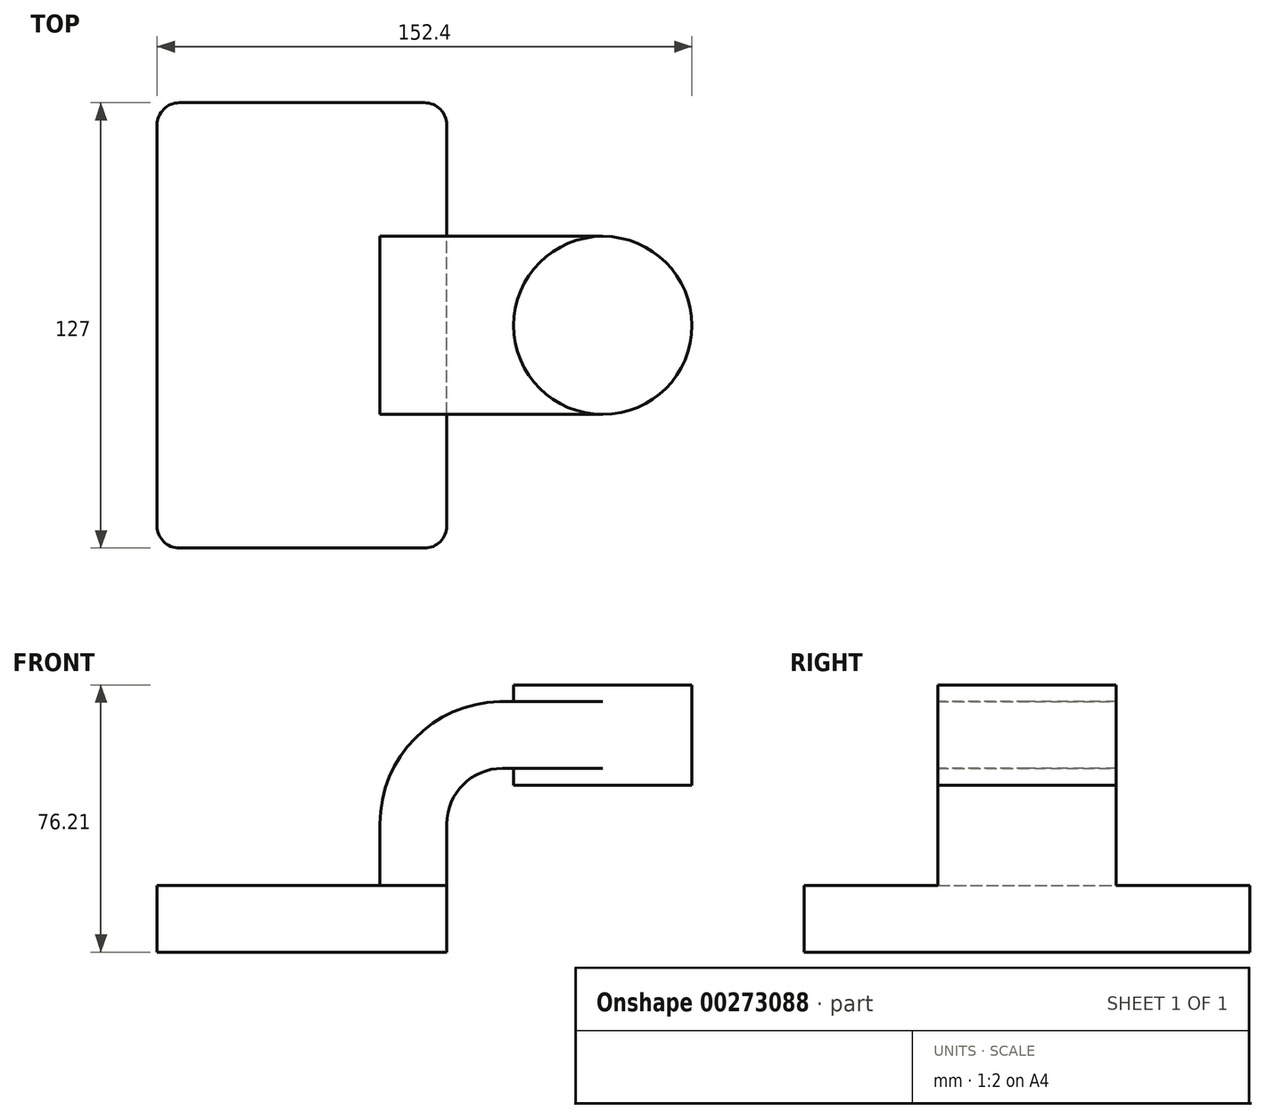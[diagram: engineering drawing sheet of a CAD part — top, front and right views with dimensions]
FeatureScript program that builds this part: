
annotation { "Feature Type Name" : "Feature", "Feature Type Description" : "" }
export const myFeature = defineFeature(function(context is Context, id is Id, definition is map)
    precondition{}
    {
        {
            var Q0;
            Q0=qCreatedBy(makeId("Front.planeOp"),FACE);
            var sketch = newSketch(context, id + "F0", { "sketchPlane" : qUnion([Q0])});
            skLineSegment(sketch, "E0.bottom", {"start": v(41.28, -9.52) * mm, "end": v(-41.28, -9.53) * mm});
            skLineSegment(sketch, "E0.top", {"start": v(41.28, 9.53) * mm, "end": v(-41.28, 9.52) * mm});
            skLineSegment(sketch, "E0.left", {"start": v(41.28, -9.52) * mm, "end": v(41.28, 9.53) * mm});
            skLineSegment(sketch, "E0.right", {"start": v(-41.28, -9.53) * mm, "end": v(-41.28, 9.52) * mm});
            skPoint(sketch, "E0.middle", {"position": v(0, 0) * mm});
            skLineSegment(sketch, "E1.bottom", {"start": v(111.12, 38.1) * mm, "end": v(60.32, 38.1) * mm});
            skLineSegment(sketch, "E1.top", {"start": v(111.12, 66.68) * mm, "end": v(60.32, 66.68) * mm});
            skLineSegment(sketch, "E1.left", {"start": v(111.12, 38.1) * mm, "end": v(111.12, 66.68) * mm});
            skLineSegment(sketch, "E1.right", {"start": v(60.32, 38.1) * mm, "end": v(60.32, 66.68) * mm});
            skPoint(sketch, "E1.middle", {"position": v(85.72, 52.39) * mm});
            skLineSegment(sketch, "E2", {"start": v(41.28, 9.53) * mm, "end": v(41.28, 27) * mm});
            skArc(sketch, "E3", {"start": v(57.15, 42.88) * mm, "mid": v(45.92, 38.23) * mm, "end": v(41.28, 27) * mm});
            skLineSegment(sketch, "E4", {"start": v(57.15, 42.88) * mm, "end": v(85.72, 42.88) * mm});
            skLineSegment(sketch, "E5.0", {"start": v(57.15, 61.93) * mm, "end": v(85.72, 61.93) * mm});
            skArc(sketch, "E5.1", {"start": v(57.15, 61.93) * mm, "mid": v(32.45, 51.7) * mm, "end": v(22.23, 27) * mm});
            skLineSegment(sketch, "E5.2", {"start": v(22.23, 9.53) * mm, "end": v(22.23, 27) * mm});
            skLineSegment(sketch, "E6", {"start": v(85.72, 38.1) * mm, "end": v(85.72, 66.68) * mm});
            skFitSpline(sketch, "E7", {"points": [v(-41.28, 9.52) * mm, v(57.15, 61.93) * mm], "startDerivative": vector(0.43, 96.05) * mm, "endDerivative": vector(141.16, 1.27) * mm});
            skSolve(sketch);
        }
        {
            var Q0;
            Q0=makeQuery(id+"F0.imprint","IMPRINT",FACE,{"disambiguationData":[TD([[makeQuery(id+"F0.imprint","IMPRINT",EDGE,{"derivedFrom":sQuery(id+"F0.wireOp",EDGE,"E0.bottom")}),-1.0]])]});
            extrude(context, id + "F1", {"entities" : qUnion([Q0]), "endBound" : BoundingType.SYMMETRIC, "depth" : 127 * mm});
        }
        {
            var Q0;
            {var subQ1=sQuery(id+"F0.wireOp",EDGE,"E2");Q0=makeQuery(id+"F0.imprint","IMPRINT",FACE,{"disambiguationData":[TD([[makeQuery(id+"F0.imprint","IMPRINT",EDGE,{"derivedFrom":subQ1}),1.0]])]});}
            var Q1;
            {var subQ0=sQuery(id+"F0.wireOp",EDGE,"E4");var subQ1=sQuery(id+"F0.wireOp",EDGE,"E1.right");var subQ2=makeQuery(id+"F0.imprint","INTERSECT",VERTEX,{"derivedFrom":[subQ1,subQ0]});Q1=makeQuery(id+"F0.imprint","IMPRINT",FACE,{"disambiguationData":[TD([[makeQuery(id+"F0.imprint","IMPRINT",EDGE,{"disambiguationData":[TD([[subQ2,-1.0]])],"derivedFrom":subQ1}),-1.0]])]});}
            extrude(context, id + "F2", {"entities" : qUnion([Q0, Q1]), "operationType" : NewBodyOperationType.ADD, "endBound" : BoundingType.SYMMETRIC, "depth" : 50.8 * mm});
        }
        {
            var Q0;
            {var subQ0=sQuery(id+"F0.wireOp",EDGE,"E1.left");Q0=makeQuery(id+"F0.imprint","IMPRINT",FACE,{"disambiguationData":[TD([[makeQuery(id+"F0.imprint","IMPRINT",EDGE,{"derivedFrom":subQ0}),1.0]])]});}
            var Q1;
            Q1=sQuery(id+"F0.wireOp",EDGE,"E6");
            revolve(context, id + "F3", {"operationType" : NewBodyOperationType.ADD, "entities" : qUnion([Q0]), "axis" : qUnion([Q1]), "revolveType" : RevolveType.FULL});
        }
        {
            var Q0;
            Q0=makeQuery(id+"F1.opExtrude","CAP_EDGE",EDGE,{"disambiguationData":[OSD([sQuery(id+"F0.wireOp",EDGE,"E0.left")])],"isStart":false});
            var Q1;
            Q1=makeQuery(id+"F1.opExtrude","CAP_EDGE",EDGE,{"disambiguationData":[OSD([sQuery(id+"F0.wireOp",EDGE,"E0.right")])],"isStart":false});
            var Q2;
            Q2=makeQuery(id+"F1.opExtrude","CAP_EDGE",EDGE,{"disambiguationData":[OSD([sQuery(id+"F0.wireOp",EDGE,"E0.right")])],"isStart":true});
            var Q3;
            Q3=makeQuery(id+"F1.opExtrude","CAP_EDGE",EDGE,{"disambiguationData":[OSD([sQuery(id+"F0.wireOp",EDGE,"E0.left")])],"isStart":true});
            fillet(context, id + "F4", {"entities" : qUnion([Q0, Q1, Q2, Q3]), "radius" : 6.35 * mm, "tangentPropagation" : true, "allowEdgeOverflow" : false});
        }
    });
